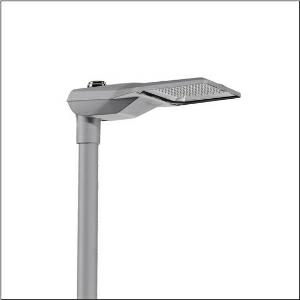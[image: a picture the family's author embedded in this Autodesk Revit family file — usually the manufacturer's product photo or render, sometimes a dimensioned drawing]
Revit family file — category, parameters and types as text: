
# Revit family: streetlight_sl_21_midi___st1_5a_5xe7p37n08lb_8b0d
name_source: partatom
category: Lighting Fixtures
units: mm (PartAtom-declared; Revit-internal decimal feet)

## family parameters
Cut with Voids When Loaded = No
Host = Face
Light Source = No
Part Type = Normal
Room Calculation Point = No
Round Connector Dimension = Use Diameter
Shared = No

## types (1)
- --- (1 x LED, 14100 lm, 98.3 W, 3000K)
    Apparent Load = 98 VA
    CIE Flux Codes = 22 53 95 100 100
    Color Rendering = 70
    Color Temperature = 3000K
    Default Elevation = 1800 mm
    Description = Streetlight SL 21 midi, mast luminaire, primary light control with lens, of PMMA, primary optical cover: cover, of toughened safety glass, transparent, light distribution: ST1.5a, light emission: direct distribution, primary light characteristic: asymmetric, installation type: side-entry, LED, 3G 2.5mm², High Power LED, rated luminous flux: 14.100lm, luminous efficacy: 143lm/W, light colour: 730, colour temperature: 3000K, control gear: NEMA (7pin), control: overheat protection, pre-setting: linear dimming characteristic, constant luminous flux control, time-dependent luminous flux control, flexible luminous flux parameterisation, mains connection: 220..240V, AC, 50/60Hz, connection cable pre-assembled, cable length: 10,5m, wiring characteristics: H05VV-F, start of lifetime: 98W, end of service life: 101W, reduction: 45W, luminaire housing, of diecast aluminium (EN AC-44300), powder-coated, SITECO metallic grey (DB 702S), corrosivity category C5 high according to DIN EN ISO 12944, multi-level sealing system, sealing non-destructively replaceable, inclination adjustable: 0°, 5°, 10°, 15°, length: 644mm, width: 335mm, height: 110mm, spigot size: 42mm (side-entry), mounting height: 4..8m, protection rating (complete): IP66, insulation class (complete): insulation class I (protective earthing), certification: CE, ENEC, ENEC+, VDE, impact resistance: IK10, permissible operating ambient temperature for outdoor applications: -40..+50°C, standard-compliant lighting for roads and squares, packaging unit: 1 piece

Light Distribution: ST1.5a
    Height = 111 mm
    Lamp = 1 x LED
    Lamp Light Flux = 14100 lm
    Lamp Power = 98.3 W
    Lamp count = 1
    Length = 644 mm
    Luminous efficacy = 143 lm/W
    Manufacturer = Siteco
    ModVariant = No
    Model = 5XE7P37N08LB
    Number of Poles = 1
    OnlyDefault = Yes
    Power Factor = 1
    Product Name = Streetlight SL 21 midi | ST1.5a
    Product group = mast luminaire | pylon top
    ProductGroupID = 6100
    Protection Class = Protection class I
    Protection Degree = IP 66
    RLX_Detail_Level = 1
    RLX_Emergency_Light_Flux = 0 lm
    RLX_Emergency_Type = 0
    RLX_Emergency_Type_DB = No
    RlxData = <blob elided: 30189 chars, md5=8aafc5e7>
    Socket = socket
    Standby Power = 0 W
    System Light Flux = 14100 lm
    System Power = 98 W
    Type Comments = factory setting: luminous flux: 100 % | dim-lin: 254 | 1020 mA
    Type Image = l_1294377.jpg
    URL = http://relux.com
    VarID = @adj_132995
    Voltage = 0 V
    Weight = 0.00 kg
    Width = 336 mm

## geometry (parser evidence)
native form markers: Blend x4, Sweep x9
no freeform markers — native parametric forms only
